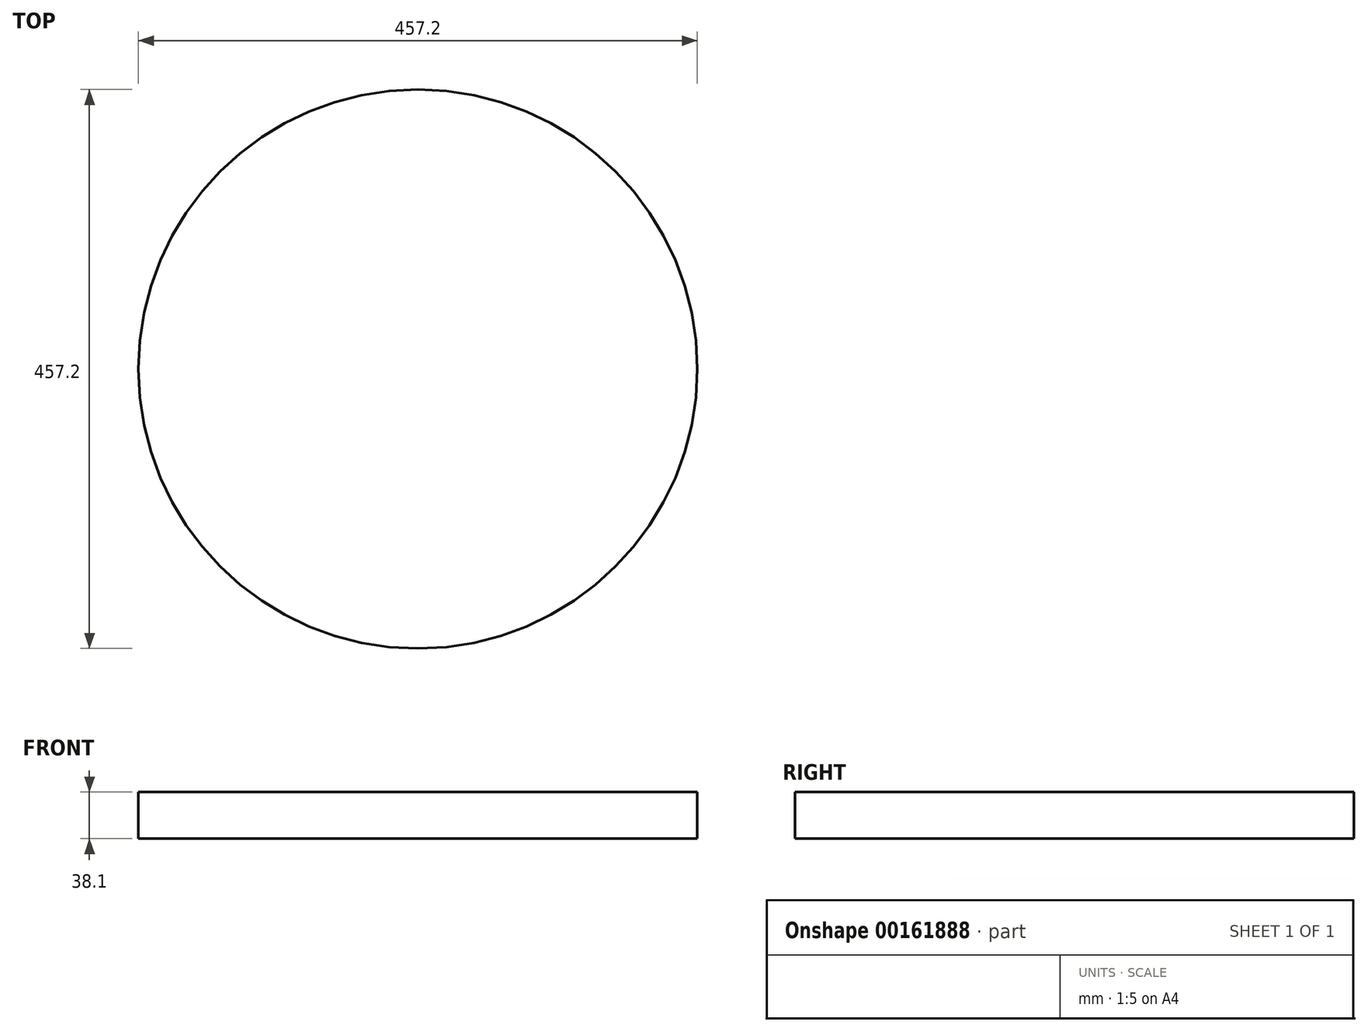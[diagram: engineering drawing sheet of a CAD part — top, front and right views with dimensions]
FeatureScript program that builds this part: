
annotation { "Feature Type Name" : "Feature", "Feature Type Description" : "" }
export const myFeature = defineFeature(function(context is Context, id is Id, definition is map)
    precondition{}
    {
        {
            var Q0;
            Q0=qCreatedBy(makeId("Top.planeOp"),FACE);
            var sketch = newSketch(context, id + "F0", { "sketchPlane" : qUnion([Q0])});
            skCircle(sketch, "E0", {"center": v(0, 0) * mm, "radius": 228.6 * mm});
            skSolve(sketch);
        }
        {
            var Q0;
            Q0=makeQuery(id+"F0.imprint","IMPRINT",FACE,{"disambiguationData":[TD([[makeQuery(id+"F0.imprint","IMPRINT",EDGE,{"derivedFrom":sQuery(id+"F0.wireOp",EDGE,"E0")}),1.0]])]});
            extrude(context, id + "F1", {"entities" : qUnion([Q0]), "depth" : 38.1 * mm});
        }
    });
